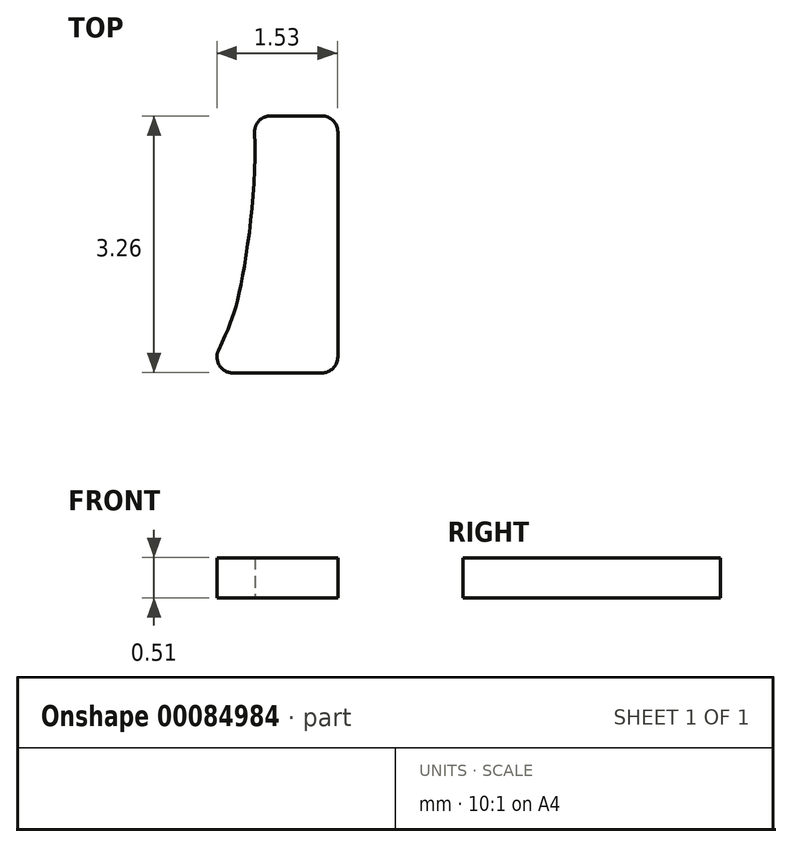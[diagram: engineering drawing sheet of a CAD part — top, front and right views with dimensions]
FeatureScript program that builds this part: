
annotation { "Feature Type Name" : "Feature", "Feature Type Description" : "" }
export const myFeature = defineFeature(function(context is Context, id is Id, definition is map)
    precondition{}
    {
        {
            var Q0;
            Q0=qCreatedBy(makeId("Top.planeOp"),FACE);
            var sketch = newSketch(context, id + "F0", { "sketchPlane" : qUnion([Q0])});
            skLineSegment(sketch, "E0", {"start": v(0.61, 1.64) * mm, "end": v(0.61, -1.62) * mm});
            skLineSegment(sketch, "E1", {"start": v(0.61, -1.62) * mm, "end": v(-1.03, -1.62) * mm});
            skFitSpline(sketch, "E2", {"points": [v(-1.03, -1.62) * mm, v(-0.65, -0.66) * mm, v(-0.45, 1.64) * mm], "startDerivative": vector(1.8, 4.1) * mm, "endDerivative": vector(-0.33, 3.95) * mm});
            skLineSegment(sketch, "E3", {"start": v(-0.45, 1.64) * mm, "end": v(0.61, 1.64) * mm});
            skSolve(sketch);
        }
        {
            var Q0;
            Q0 = qSketchRegion(id + "F0", true);
            var Q1;
            Q1=sQuery(id+"F0.wireOp",EDGE,"E0");
            var Q2;
            Q2=sQuery(id+"F0.wireOp",EDGE,"E1");
            var Q3;
            Q3=sQuery(id+"F0.wireOp",EDGE,"E2");
            var Q4;
            Q4=sQuery(id+"F0.wireOp",EDGE,"E3");
            extrude(context, id + "F1", {"entities" : qUnion([Q0]), "surfaceEntities" : qUnion([Q1, Q2, Q3, Q4]), "depth" : 0.5 * mm});
        }
        {
            var Q0;
            Q0=makeQuery(id+"F1.opExtrude","SWEPT_EDGE",EDGE,{"disambiguationData":[OSD([sQuery(id+"F0.wireOp",EDGE,"E1"),sQuery(id+"F0.wireOp",EDGE,"E2")])]});
            var Q1;
            Q1=makeQuery(id+"F1.opExtrude","SWEPT_EDGE",EDGE,{"disambiguationData":[OSD([sQuery(id+"F0.wireOp",EDGE,"E2"),sQuery(id+"F0.wireOp",EDGE,"E3")])]});
            var Q2;
            Q2=makeQuery(id+"F1.opExtrude","SWEPT_EDGE",EDGE,{"disambiguationData":[OSD([sQuery(id+"F0.wireOp",EDGE,"E0"),sQuery(id+"F0.wireOp",EDGE,"E1")])]});
            var Q3;
            Q3=makeQuery(id+"F1.opExtrude","SWEPT_EDGE",EDGE,{"disambiguationData":[OSD([sQuery(id+"F0.wireOp",EDGE,"E0"),sQuery(id+"F0.wireOp",EDGE,"E3")])]});
            fillet(context, id + "F2", {"entities" : qUnion([Q0, Q1, Q2, Q3]), "radius" : 0.2 * mm, "tangentPropagation" : true, "allowEdgeOverflow" : false});
        }
    });
